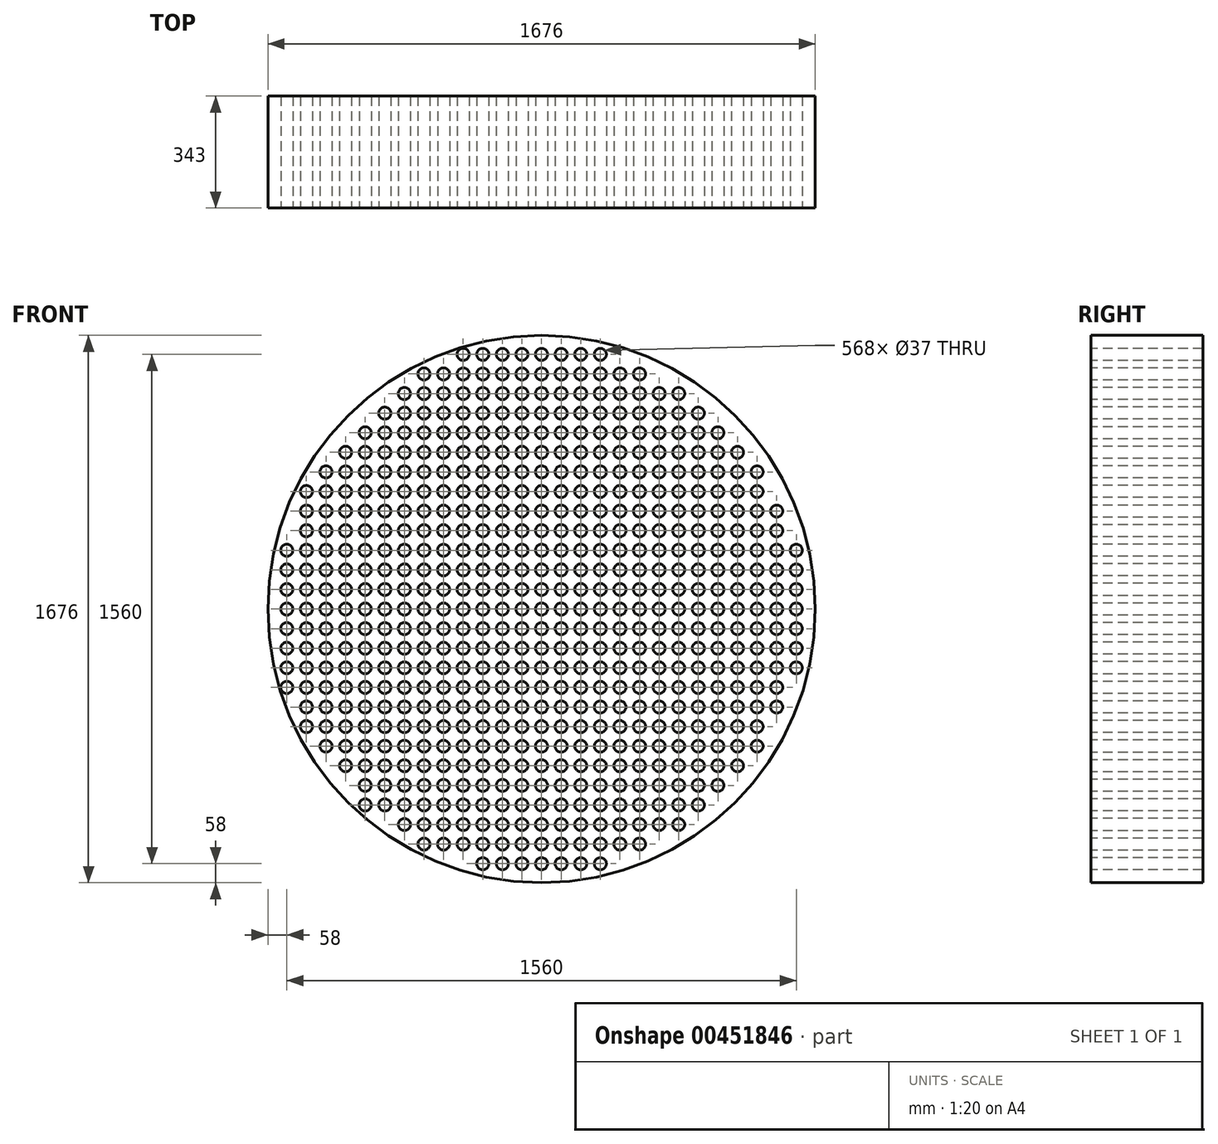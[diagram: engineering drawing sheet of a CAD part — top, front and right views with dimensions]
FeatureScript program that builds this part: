
annotation { "Feature Type Name" : "Feature", "Feature Type Description" : "" }
export const myFeature = defineFeature(function(context is Context, id is Id, definition is map)
    precondition{}
    {
        {
            var Q0;
            Q0=qCreatedBy(makeId("Front.planeOp"),FACE);
            var sketch = newSketch(context, id + "F0", { "sketchPlane" : qUnion([Q0])});
            skCircle(sketch, "E0", {"center": v(0, 0) * mm, "radius": 838 * mm});
            skSolve(sketch);
        }
        {
            var Q0;
            Q0 = qSketchRegion(id + "F0", true);
            extrude(context, id + "F1", {"entities" : qUnion([Q0]), "oppositeDirection" : true, "depth" : 343 * mm});
        }
        {
            var Q0;
            Q0=makeQuery(id+"F1.opExtrude","CAP_FACE",FACE,{"disambiguationData":[OSD([sQuery(id+"F0.wireOp",EDGE,"E0")])],"isStart":true});
            var sketch = newSketch(context, id + "F2", { "sketchPlane" : qUnion([Q0])});
            skCircle(sketch, "E1", {"center": v(0, 0) * mm, "radius": 18.5 * mm});
            skCircle(sketch, "E2.0.1.0", {"center": v(0, 60) * mm, "radius": 18.5 * mm});
            skCircle(sketch, "E2.0.2.0", {"center": v(0, 120) * mm, "radius": 18.5 * mm});
            skCircle(sketch, "E2.0.3.0", {"center": v(0, 180) * mm, "radius": 18.5 * mm});
            skCircle(sketch, "E2.0.4.0", {"center": v(0, 240) * mm, "radius": 18.5 * mm});
            skCircle(sketch, "E2.0.5.0", {"center": v(0, 300) * mm, "radius": 18.5 * mm});
            skCircle(sketch, "E2.0.6.0", {"center": v(0, 360) * mm, "radius": 18.5 * mm});
            skCircle(sketch, "E2.0.7.0", {"center": v(0, 420) * mm, "radius": 18.5 * mm});
            skCircle(sketch, "E2.0.8.0", {"center": v(0, 480) * mm, "radius": 18.5 * mm});
            skCircle(sketch, "E2.0.9.0", {"center": v(0, 540) * mm, "radius": 18.5 * mm});
            skCircle(sketch, "E2.0.10.0", {"center": v(0, 600) * mm, "radius": 18.5 * mm});
            skCircle(sketch, "E2.0.11.0", {"center": v(0, 660) * mm, "radius": 18.5 * mm});
            skCircle(sketch, "E2.0.12.0", {"center": v(0, 720) * mm, "radius": 18.5 * mm});
            skCircle(sketch, "E2.0.13.0", {"center": v(0, 780) * mm, "radius": 18.5 * mm});
            skCircle(sketch, "E2.1.0.0", {"center": v(60, 0) * mm, "radius": 18.5 * mm});
            skCircle(sketch, "E2.1.1.0", {"center": v(60, 60) * mm, "radius": 18.5 * mm});
            skCircle(sketch, "E2.1.2.0", {"center": v(60, 120) * mm, "radius": 18.5 * mm});
            skCircle(sketch, "E2.1.3.0", {"center": v(60, 180) * mm, "radius": 18.5 * mm});
            skCircle(sketch, "E2.1.4.0", {"center": v(60, 240) * mm, "radius": 18.5 * mm});
            skCircle(sketch, "E2.1.5.0", {"center": v(60, 300) * mm, "radius": 18.5 * mm});
            skCircle(sketch, "E2.1.6.0", {"center": v(60, 360) * mm, "radius": 18.5 * mm});
            skCircle(sketch, "E2.1.7.0", {"center": v(60, 420) * mm, "radius": 18.5 * mm});
            skCircle(sketch, "E2.1.8.0", {"center": v(60, 480) * mm, "radius": 18.5 * mm});
            skCircle(sketch, "E2.1.9.0", {"center": v(60, 540) * mm, "radius": 18.5 * mm});
            skCircle(sketch, "E2.1.10.0", {"center": v(60, 600) * mm, "radius": 18.5 * mm});
            skCircle(sketch, "E2.1.11.0", {"center": v(60, 660) * mm, "radius": 18.5 * mm});
            skCircle(sketch, "E2.1.12.0", {"center": v(60, 720) * mm, "radius": 18.5 * mm});
            skCircle(sketch, "E2.1.13.0", {"center": v(60, 780) * mm, "radius": 18.5 * mm});
            skCircle(sketch, "E2.2.0.0", {"center": v(120, 0) * mm, "radius": 18.5 * mm});
            skCircle(sketch, "E2.2.1.0", {"center": v(120, 60) * mm, "radius": 18.5 * mm});
            skCircle(sketch, "E2.2.2.0", {"center": v(120, 120) * mm, "radius": 18.5 * mm});
            skCircle(sketch, "E2.2.3.0", {"center": v(120, 180) * mm, "radius": 18.5 * mm});
            skCircle(sketch, "E2.2.4.0", {"center": v(120, 240) * mm, "radius": 18.5 * mm});
            skCircle(sketch, "E2.2.5.0", {"center": v(120, 300) * mm, "radius": 18.5 * mm});
            skCircle(sketch, "E2.2.6.0", {"center": v(120, 360) * mm, "radius": 18.5 * mm});
            skCircle(sketch, "E2.2.7.0", {"center": v(120, 420) * mm, "radius": 18.5 * mm});
            skCircle(sketch, "E2.2.8.0", {"center": v(120, 480) * mm, "radius": 18.5 * mm});
            skCircle(sketch, "E2.2.9.0", {"center": v(120, 540) * mm, "radius": 18.5 * mm});
            skCircle(sketch, "E2.2.10.0", {"center": v(120, 600) * mm, "radius": 18.5 * mm});
            skCircle(sketch, "E2.2.11.0", {"center": v(120, 660) * mm, "radius": 18.5 * mm});
            skCircle(sketch, "E2.2.12.0", {"center": v(120, 720) * mm, "radius": 18.5 * mm});
            skCircle(sketch, "E2.2.13.0", {"center": v(120, 780) * mm, "radius": 18.5 * mm});
            skCircle(sketch, "E2.3.0.0", {"center": v(180, 0) * mm, "radius": 18.5 * mm});
            skCircle(sketch, "E2.3.1.0", {"center": v(180, 60) * mm, "radius": 18.5 * mm});
            skCircle(sketch, "E2.3.2.0", {"center": v(180, 120) * mm, "radius": 18.5 * mm});
            skCircle(sketch, "E2.3.3.0", {"center": v(180, 180) * mm, "radius": 18.5 * mm});
            skCircle(sketch, "E2.3.4.0", {"center": v(180, 240) * mm, "radius": 18.5 * mm});
            skCircle(sketch, "E2.3.5.0", {"center": v(180, 300) * mm, "radius": 18.5 * mm});
            skCircle(sketch, "E2.3.6.0", {"center": v(180, 360) * mm, "radius": 18.5 * mm});
            skCircle(sketch, "E2.3.7.0", {"center": v(180, 420) * mm, "radius": 18.5 * mm});
            skCircle(sketch, "E2.3.8.0", {"center": v(180, 480) * mm, "radius": 18.5 * mm});
            skCircle(sketch, "E2.3.9.0", {"center": v(180, 540) * mm, "radius": 18.5 * mm});
            skCircle(sketch, "E2.3.10.0", {"center": v(180, 600) * mm, "radius": 18.5 * mm});
            skCircle(sketch, "E2.3.11.0", {"center": v(180, 660) * mm, "radius": 18.5 * mm});
            skCircle(sketch, "E2.3.12.0", {"center": v(180, 720) * mm, "radius": 18.5 * mm});
            skCircle(sketch, "E2.3.13.0", {"center": v(180, 780) * mm, "radius": 18.5 * mm});
            skCircle(sketch, "E2.4.0.0", {"center": v(240, 0) * mm, "radius": 18.5 * mm});
            skCircle(sketch, "E2.4.1.0", {"center": v(240, 60) * mm, "radius": 18.5 * mm});
            skCircle(sketch, "E2.4.2.0", {"center": v(240, 120) * mm, "radius": 18.5 * mm});
            skCircle(sketch, "E2.4.3.0", {"center": v(240, 180) * mm, "radius": 18.5 * mm});
            skCircle(sketch, "E2.4.4.0", {"center": v(240, 240) * mm, "radius": 18.5 * mm});
            skCircle(sketch, "E2.4.5.0", {"center": v(240, 300) * mm, "radius": 18.5 * mm});
            skCircle(sketch, "E2.4.6.0", {"center": v(240, 360) * mm, "radius": 18.5 * mm});
            skCircle(sketch, "E2.4.7.0", {"center": v(240, 420) * mm, "radius": 18.5 * mm});
            skCircle(sketch, "E2.4.8.0", {"center": v(240, 480) * mm, "radius": 18.5 * mm});
            skCircle(sketch, "E2.4.9.0", {"center": v(240, 540) * mm, "radius": 18.5 * mm});
            skCircle(sketch, "E2.4.10.0", {"center": v(240, 600) * mm, "radius": 18.5 * mm});
            skCircle(sketch, "E2.4.11.0", {"center": v(240, 660) * mm, "radius": 18.5 * mm});
            skCircle(sketch, "E2.4.12.0", {"center": v(240, 720) * mm, "radius": 18.5 * mm});
            skCircle(sketch, "E2.5.0.0", {"center": v(300, 0) * mm, "radius": 18.5 * mm});
            skCircle(sketch, "E2.5.1.0", {"center": v(300, 60) * mm, "radius": 18.5 * mm});
            skCircle(sketch, "E2.5.2.0", {"center": v(300, 120) * mm, "radius": 18.5 * mm});
            skCircle(sketch, "E2.5.3.0", {"center": v(300, 180) * mm, "radius": 18.5 * mm});
            skCircle(sketch, "E2.5.4.0", {"center": v(300, 240) * mm, "radius": 18.5 * mm});
            skCircle(sketch, "E2.5.5.0", {"center": v(300, 300) * mm, "radius": 18.5 * mm});
            skCircle(sketch, "E2.5.6.0", {"center": v(300, 360) * mm, "radius": 18.5 * mm});
            skCircle(sketch, "E2.5.7.0", {"center": v(300, 420) * mm, "radius": 18.5 * mm});
            skCircle(sketch, "E2.5.8.0", {"center": v(300, 480) * mm, "radius": 18.5 * mm});
            skCircle(sketch, "E2.5.9.0", {"center": v(300, 540) * mm, "radius": 18.5 * mm});
            skCircle(sketch, "E2.5.10.0", {"center": v(300, 600) * mm, "radius": 18.5 * mm});
            skCircle(sketch, "E2.5.11.0", {"center": v(300, 660) * mm, "radius": 18.5 * mm});
            skCircle(sketch, "E2.5.12.0", {"center": v(300, 720) * mm, "radius": 18.5 * mm});
            skCircle(sketch, "E2.6.0.0", {"center": v(360, 0) * mm, "radius": 18.5 * mm});
            skCircle(sketch, "E2.6.1.0", {"center": v(360, 60) * mm, "radius": 18.5 * mm});
            skCircle(sketch, "E2.6.2.0", {"center": v(360, 120) * mm, "radius": 18.5 * mm});
            skCircle(sketch, "E2.6.3.0", {"center": v(360, 180) * mm, "radius": 18.5 * mm});
            skCircle(sketch, "E2.6.4.0", {"center": v(360, 240) * mm, "radius": 18.5 * mm});
            skCircle(sketch, "E2.6.5.0", {"center": v(360, 300) * mm, "radius": 18.5 * mm});
            skCircle(sketch, "E2.6.6.0", {"center": v(360, 360) * mm, "radius": 18.5 * mm});
            skCircle(sketch, "E2.6.7.0", {"center": v(360, 420) * mm, "radius": 18.5 * mm});
            skCircle(sketch, "E2.6.8.0", {"center": v(360, 480) * mm, "radius": 18.5 * mm});
            skCircle(sketch, "E2.6.9.0", {"center": v(360, 540) * mm, "radius": 18.5 * mm});
            skCircle(sketch, "E2.6.10.0", {"center": v(360, 600) * mm, "radius": 18.5 * mm});
            skCircle(sketch, "E2.6.11.0", {"center": v(360, 660) * mm, "radius": 18.5 * mm});
            skCircle(sketch, "E2.7.0.0", {"center": v(420, 0) * mm, "radius": 18.5 * mm});
            skCircle(sketch, "E2.7.1.0", {"center": v(420, 60) * mm, "radius": 18.5 * mm});
            skCircle(sketch, "E2.7.2.0", {"center": v(420, 120) * mm, "radius": 18.5 * mm});
            skCircle(sketch, "E2.7.3.0", {"center": v(420, 180) * mm, "radius": 18.5 * mm});
            skCircle(sketch, "E2.7.4.0", {"center": v(420, 240) * mm, "radius": 18.5 * mm});
            skCircle(sketch, "E2.7.5.0", {"center": v(420, 300) * mm, "radius": 18.5 * mm});
            skCircle(sketch, "E2.7.6.0", {"center": v(420, 360) * mm, "radius": 18.5 * mm});
            skCircle(sketch, "E2.7.7.0", {"center": v(420, 420) * mm, "radius": 18.5 * mm});
            skCircle(sketch, "E2.7.8.0", {"center": v(420, 480) * mm, "radius": 18.5 * mm});
            skCircle(sketch, "E2.7.9.0", {"center": v(420, 540) * mm, "radius": 18.5 * mm});
            skCircle(sketch, "E2.7.10.0", {"center": v(420, 600) * mm, "radius": 18.5 * mm});
            skCircle(sketch, "E2.7.11.0", {"center": v(420, 660) * mm, "radius": 18.5 * mm});
            skCircle(sketch, "E2.8.0.0", {"center": v(480, 0) * mm, "radius": 18.5 * mm});
            skCircle(sketch, "E2.8.1.0", {"center": v(480, 60) * mm, "radius": 18.5 * mm});
            skCircle(sketch, "E2.8.2.0", {"center": v(480, 120) * mm, "radius": 18.5 * mm});
            skCircle(sketch, "E2.8.3.0", {"center": v(480, 180) * mm, "radius": 18.5 * mm});
            skCircle(sketch, "E2.8.4.0", {"center": v(480, 240) * mm, "radius": 18.5 * mm});
            skCircle(sketch, "E2.8.5.0", {"center": v(480, 300) * mm, "radius": 18.5 * mm});
            skCircle(sketch, "E2.8.6.0", {"center": v(480, 360) * mm, "radius": 18.5 * mm});
            skCircle(sketch, "E2.8.7.0", {"center": v(480, 420) * mm, "radius": 18.5 * mm});
            skCircle(sketch, "E2.8.8.0", {"center": v(480, 480) * mm, "radius": 18.5 * mm});
            skCircle(sketch, "E2.8.9.0", {"center": v(480, 540) * mm, "radius": 18.5 * mm});
            skCircle(sketch, "E2.8.10.0", {"center": v(480, 600) * mm, "radius": 18.5 * mm});
            skCircle(sketch, "E2.9.0.0", {"center": v(540, 0) * mm, "radius": 18.5 * mm});
            skCircle(sketch, "E2.9.1.0", {"center": v(540, 60) * mm, "radius": 18.5 * mm});
            skCircle(sketch, "E2.9.2.0", {"center": v(540, 120) * mm, "radius": 18.5 * mm});
            skCircle(sketch, "E2.9.3.0", {"center": v(540, 180) * mm, "radius": 18.5 * mm});
            skCircle(sketch, "E2.9.4.0", {"center": v(540, 240) * mm, "radius": 18.5 * mm});
            skCircle(sketch, "E2.9.5.0", {"center": v(540, 300) * mm, "radius": 18.5 * mm});
            skCircle(sketch, "E2.9.6.0", {"center": v(540, 360) * mm, "radius": 18.5 * mm});
            skCircle(sketch, "E2.9.7.0", {"center": v(540, 420) * mm, "radius": 18.5 * mm});
            skCircle(sketch, "E2.9.8.0", {"center": v(540, 480) * mm, "radius": 18.5 * mm});
            skCircle(sketch, "E2.9.9.0", {"center": v(540, 540) * mm, "radius": 18.5 * mm});
            skCircle(sketch, "E2.10.0.0", {"center": v(600, 0) * mm, "radius": 18.5 * mm});
            skCircle(sketch, "E2.10.1.0", {"center": v(600, 60) * mm, "radius": 18.5 * mm});
            skCircle(sketch, "E2.10.2.0", {"center": v(600, 120) * mm, "radius": 18.5 * mm});
            skCircle(sketch, "E2.10.3.0", {"center": v(600, 180) * mm, "radius": 18.5 * mm});
            skCircle(sketch, "E2.10.4.0", {"center": v(600, 240) * mm, "radius": 18.5 * mm});
            skCircle(sketch, "E2.10.5.0", {"center": v(600, 300) * mm, "radius": 18.5 * mm});
            skCircle(sketch, "E2.10.6.0", {"center": v(600, 360) * mm, "radius": 18.5 * mm});
            skCircle(sketch, "E2.10.7.0", {"center": v(600, 420) * mm, "radius": 18.5 * mm});
            skCircle(sketch, "E2.10.8.0", {"center": v(600, 480) * mm, "radius": 18.5 * mm});
            skCircle(sketch, "E2.11.0.0", {"center": v(660, 0) * mm, "radius": 18.5 * mm});
            skCircle(sketch, "E2.11.1.0", {"center": v(660, 60) * mm, "radius": 18.5 * mm});
            skCircle(sketch, "E2.11.2.0", {"center": v(660, 120) * mm, "radius": 18.5 * mm});
            skCircle(sketch, "E2.11.3.0", {"center": v(660, 180) * mm, "radius": 18.5 * mm});
            skCircle(sketch, "E2.11.4.0", {"center": v(660, 240) * mm, "radius": 18.5 * mm});
            skCircle(sketch, "E2.11.5.0", {"center": v(660, 300) * mm, "radius": 18.5 * mm});
            skCircle(sketch, "E2.11.6.0", {"center": v(660, 360) * mm, "radius": 18.5 * mm});
            skCircle(sketch, "E2.11.7.0", {"center": v(660, 420) * mm, "radius": 18.5 * mm});
            skCircle(sketch, "E2.12.0.0", {"center": v(720, 0) * mm, "radius": 18.5 * mm});
            skCircle(sketch, "E2.12.1.0", {"center": v(720, 60) * mm, "radius": 18.5 * mm});
            skCircle(sketch, "E2.12.2.0", {"center": v(720, 120) * mm, "radius": 18.5 * mm});
            skCircle(sketch, "E2.12.3.0", {"center": v(720, 180) * mm, "radius": 18.5 * mm});
            skCircle(sketch, "E2.12.4.0", {"center": v(720, 240) * mm, "radius": 18.5 * mm});
            skCircle(sketch, "E2.12.5.0", {"center": v(720, 300) * mm, "radius": 18.5 * mm});
            skCircle(sketch, "E2.13.0.0", {"center": v(780, 0) * mm, "radius": 18.5 * mm});
            skCircle(sketch, "E2.13.1.0", {"center": v(780, 60) * mm, "radius": 18.5 * mm});
            skCircle(sketch, "E2.13.2.0", {"center": v(780, 120) * mm, "radius": 18.5 * mm});
            skCircle(sketch, "E2.13.3.0", {"center": v(780, 180) * mm, "radius": 18.5 * mm});
            skLineSegment(sketch, "E2.direction1", {"start": v(0, 0) * mm, "end": v(60, 0) * mm, "construction": true});
            skLineSegment(sketch, "E2.direction2", {"start": v(0, 0) * mm, "end": v(0, 60) * mm, "construction": true});
            skCircle(sketch, "E3.0.1.0", {"center": v(0, -60) * mm, "radius": 18.5 * mm});
            skCircle(sketch, "E3.0.2.0", {"center": v(0, -120) * mm, "radius": 18.5 * mm});
            skCircle(sketch, "E3.0.3.0", {"center": v(0, -180) * mm, "radius": 18.5 * mm});
            skCircle(sketch, "E3.0.4.0", {"center": v(0, -240) * mm, "radius": 18.5 * mm});
            skCircle(sketch, "E3.0.5.0", {"center": v(0, -300) * mm, "radius": 18.5 * mm});
            skCircle(sketch, "E3.0.6.0", {"center": v(0, -360) * mm, "radius": 18.5 * mm});
            skCircle(sketch, "E3.0.7.0", {"center": v(0, -420) * mm, "radius": 18.5 * mm});
            skCircle(sketch, "E3.0.8.0", {"center": v(0, -480) * mm, "radius": 18.5 * mm});
            skCircle(sketch, "E3.0.9.0", {"center": v(0, -540) * mm, "radius": 18.5 * mm});
            skCircle(sketch, "E3.0.10.0", {"center": v(0, -600) * mm, "radius": 18.5 * mm});
            skCircle(sketch, "E3.0.11.0", {"center": v(0, -660) * mm, "radius": 18.5 * mm});
            skCircle(sketch, "E3.0.12.0", {"center": v(0, -720) * mm, "radius": 18.5 * mm});
            skCircle(sketch, "E3.0.13.0", {"center": v(0, -780) * mm, "radius": 18.5 * mm});
            skCircle(sketch, "E3.1.0.0", {"center": v(-60, 0) * mm, "radius": 18.5 * mm});
            skCircle(sketch, "E3.1.1.0", {"center": v(-60, -60) * mm, "radius": 18.5 * mm});
            skCircle(sketch, "E3.1.2.0", {"center": v(-60, -120) * mm, "radius": 18.5 * mm});
            skCircle(sketch, "E3.1.3.0", {"center": v(-60, -180) * mm, "radius": 18.5 * mm});
            skCircle(sketch, "E3.1.4.0", {"center": v(-60, -240) * mm, "radius": 18.5 * mm});
            skCircle(sketch, "E3.1.5.0", {"center": v(-60, -300) * mm, "radius": 18.5 * mm});
            skCircle(sketch, "E3.1.6.0", {"center": v(-60, -360) * mm, "radius": 18.5 * mm});
            skCircle(sketch, "E3.1.7.0", {"center": v(-60, -420) * mm, "radius": 18.5 * mm});
            skCircle(sketch, "E3.1.8.0", {"center": v(-60, -480) * mm, "radius": 18.5 * mm});
            skCircle(sketch, "E3.1.9.0", {"center": v(-60, -540) * mm, "radius": 18.5 * mm});
            skCircle(sketch, "E3.1.10.0", {"center": v(-60, -600) * mm, "radius": 18.5 * mm});
            skCircle(sketch, "E3.1.11.0", {"center": v(-60, -660) * mm, "radius": 18.5 * mm});
            skCircle(sketch, "E3.1.12.0", {"center": v(-60, -720) * mm, "radius": 18.5 * mm});
            skCircle(sketch, "E3.1.13.0", {"center": v(-60, -780) * mm, "radius": 18.5 * mm});
            skCircle(sketch, "E3.2.0.0", {"center": v(-120, 0) * mm, "radius": 18.5 * mm});
            skCircle(sketch, "E3.2.1.0", {"center": v(-120, -60) * mm, "radius": 18.5 * mm});
            skCircle(sketch, "E3.2.2.0", {"center": v(-120, -120) * mm, "radius": 18.5 * mm});
            skCircle(sketch, "E3.2.3.0", {"center": v(-120, -180) * mm, "radius": 18.5 * mm});
            skCircle(sketch, "E3.2.4.0", {"center": v(-120, -240) * mm, "radius": 18.5 * mm});
            skCircle(sketch, "E3.2.5.0", {"center": v(-120, -300) * mm, "radius": 18.5 * mm});
            skCircle(sketch, "E3.2.6.0", {"center": v(-120, -360) * mm, "radius": 18.5 * mm});
            skCircle(sketch, "E3.2.7.0", {"center": v(-120, -420) * mm, "radius": 18.5 * mm});
            skCircle(sketch, "E3.2.8.0", {"center": v(-120, -480) * mm, "radius": 18.5 * mm});
            skCircle(sketch, "E3.2.9.0", {"center": v(-120, -540) * mm, "radius": 18.5 * mm});
            skCircle(sketch, "E3.2.10.0", {"center": v(-120, -600) * mm, "radius": 18.5 * mm});
            skCircle(sketch, "E3.2.11.0", {"center": v(-120, -660) * mm, "radius": 18.5 * mm});
            skCircle(sketch, "E3.2.12.0", {"center": v(-120, -720) * mm, "radius": 18.5 * mm});
            skCircle(sketch, "E3.2.13.0", {"center": v(-120, -780) * mm, "radius": 18.5 * mm});
            skCircle(sketch, "E3.3.0.0", {"center": v(-180, 0) * mm, "radius": 18.5 * mm});
            skCircle(sketch, "E3.3.1.0", {"center": v(-180, -60) * mm, "radius": 18.5 * mm});
            skCircle(sketch, "E3.3.2.0", {"center": v(-180, -120) * mm, "radius": 18.5 * mm});
            skCircle(sketch, "E3.3.3.0", {"center": v(-180, -180) * mm, "radius": 18.5 * mm});
            skCircle(sketch, "E3.3.4.0", {"center": v(-180, -240) * mm, "radius": 18.5 * mm});
            skCircle(sketch, "E3.3.5.0", {"center": v(-180, -300) * mm, "radius": 18.5 * mm});
            skCircle(sketch, "E3.3.6.0", {"center": v(-180, -360) * mm, "radius": 18.5 * mm});
            skCircle(sketch, "E3.3.7.0", {"center": v(-180, -420) * mm, "radius": 18.5 * mm});
            skCircle(sketch, "E3.3.8.0", {"center": v(-180, -480) * mm, "radius": 18.5 * mm});
            skCircle(sketch, "E3.3.9.0", {"center": v(-180, -540) * mm, "radius": 18.5 * mm});
            skCircle(sketch, "E3.3.10.0", {"center": v(-180, -600) * mm, "radius": 18.5 * mm});
            skCircle(sketch, "E3.3.11.0", {"center": v(-180, -660) * mm, "radius": 18.5 * mm});
            skCircle(sketch, "E3.3.12.0", {"center": v(-180, -720) * mm, "radius": 18.5 * mm});
            skCircle(sketch, "E3.3.13.0", {"center": v(-180, -780) * mm, "radius": 18.5 * mm});
            skCircle(sketch, "E3.4.0.0", {"center": v(-240, 0) * mm, "radius": 18.5 * mm});
            skCircle(sketch, "E3.4.1.0", {"center": v(-240, -60) * mm, "radius": 18.5 * mm});
            skCircle(sketch, "E3.4.2.0", {"center": v(-240, -120) * mm, "radius": 18.5 * mm});
            skCircle(sketch, "E3.4.3.0", {"center": v(-240, -180) * mm, "radius": 18.5 * mm});
            skCircle(sketch, "E3.4.4.0", {"center": v(-240, -240) * mm, "radius": 18.5 * mm});
            skCircle(sketch, "E3.4.5.0", {"center": v(-240, -300) * mm, "radius": 18.5 * mm});
            skCircle(sketch, "E3.4.6.0", {"center": v(-240, -360) * mm, "radius": 18.5 * mm});
            skCircle(sketch, "E3.4.7.0", {"center": v(-240, -420) * mm, "radius": 18.5 * mm});
            skCircle(sketch, "E3.4.8.0", {"center": v(-240, -480) * mm, "radius": 18.5 * mm});
            skCircle(sketch, "E3.4.9.0", {"center": v(-240, -540) * mm, "radius": 18.5 * mm});
            skCircle(sketch, "E3.4.10.0", {"center": v(-240, -600) * mm, "radius": 18.5 * mm});
            skCircle(sketch, "E3.4.11.0", {"center": v(-240, -660) * mm, "radius": 18.5 * mm});
            skCircle(sketch, "E3.4.12.0", {"center": v(-240, -720) * mm, "radius": 18.5 * mm});
            skCircle(sketch, "E3.5.0.0", {"center": v(-300, 0) * mm, "radius": 18.5 * mm});
            skCircle(sketch, "E3.5.1.0", {"center": v(-300, -60) * mm, "radius": 18.5 * mm});
            skCircle(sketch, "E3.5.2.0", {"center": v(-300, -120) * mm, "radius": 18.5 * mm});
            skCircle(sketch, "E3.5.3.0", {"center": v(-300, -180) * mm, "radius": 18.5 * mm});
            skCircle(sketch, "E3.5.4.0", {"center": v(-300, -240) * mm, "radius": 18.5 * mm});
            skCircle(sketch, "E3.5.5.0", {"center": v(-300, -300) * mm, "radius": 18.5 * mm});
            skCircle(sketch, "E3.5.6.0", {"center": v(-300, -360) * mm, "radius": 18.5 * mm});
            skCircle(sketch, "E3.5.7.0", {"center": v(-300, -420) * mm, "radius": 18.5 * mm});
            skCircle(sketch, "E3.5.8.0", {"center": v(-300, -480) * mm, "radius": 18.5 * mm});
            skCircle(sketch, "E3.5.9.0", {"center": v(-300, -540) * mm, "radius": 18.5 * mm});
            skCircle(sketch, "E3.5.10.0", {"center": v(-300, -600) * mm, "radius": 18.5 * mm});
            skCircle(sketch, "E3.5.11.0", {"center": v(-300, -660) * mm, "radius": 18.5 * mm});
            skCircle(sketch, "E3.5.12.0", {"center": v(-300, -720) * mm, "radius": 18.5 * mm});
            skCircle(sketch, "E3.6.0.0", {"center": v(-360, 0) * mm, "radius": 18.5 * mm});
            skCircle(sketch, "E3.6.1.0", {"center": v(-360, -60) * mm, "radius": 18.5 * mm});
            skCircle(sketch, "E3.6.2.0", {"center": v(-360, -120) * mm, "radius": 18.5 * mm});
            skCircle(sketch, "E3.6.3.0", {"center": v(-360, -180) * mm, "radius": 18.5 * mm});
            skCircle(sketch, "E3.6.4.0", {"center": v(-360, -240) * mm, "radius": 18.5 * mm});
            skCircle(sketch, "E3.6.5.0", {"center": v(-360, -300) * mm, "radius": 18.5 * mm});
            skCircle(sketch, "E3.6.6.0", {"center": v(-360, -360) * mm, "radius": 18.5 * mm});
            skCircle(sketch, "E3.6.7.0", {"center": v(-360, -420) * mm, "radius": 18.5 * mm});
            skCircle(sketch, "E3.6.8.0", {"center": v(-360, -480) * mm, "radius": 18.5 * mm});
            skCircle(sketch, "E3.6.9.0", {"center": v(-360, -540) * mm, "radius": 18.5 * mm});
            skCircle(sketch, "E3.6.10.0", {"center": v(-360, -600) * mm, "radius": 18.5 * mm});
            skCircle(sketch, "E3.6.11.0", {"center": v(-360, -660) * mm, "radius": 18.5 * mm});
            skCircle(sketch, "E3.6.12.0", {"center": v(-360, -720) * mm, "radius": 18.5 * mm});
            skCircle(sketch, "E3.7.0.0", {"center": v(-420, 0) * mm, "radius": 18.5 * mm});
            skCircle(sketch, "E3.7.1.0", {"center": v(-420, -60) * mm, "radius": 18.5 * mm});
            skCircle(sketch, "E3.7.2.0", {"center": v(-420, -120) * mm, "radius": 18.5 * mm});
            skCircle(sketch, "E3.7.3.0", {"center": v(-420, -180) * mm, "radius": 18.5 * mm});
            skCircle(sketch, "E3.7.4.0", {"center": v(-420, -240) * mm, "radius": 18.5 * mm});
            skCircle(sketch, "E3.7.5.0", {"center": v(-420, -300) * mm, "radius": 18.5 * mm});
            skCircle(sketch, "E3.7.6.0", {"center": v(-420, -360) * mm, "radius": 18.5 * mm});
            skCircle(sketch, "E3.7.7.0", {"center": v(-420, -420) * mm, "radius": 18.5 * mm});
            skCircle(sketch, "E3.7.8.0", {"center": v(-420, -480) * mm, "radius": 18.5 * mm});
            skCircle(sketch, "E3.7.9.0", {"center": v(-420, -540) * mm, "radius": 18.5 * mm});
            skCircle(sketch, "E3.7.10.0", {"center": v(-420, -600) * mm, "radius": 18.5 * mm});
            skCircle(sketch, "E3.7.11.0", {"center": v(-420, -660) * mm, "radius": 18.5 * mm});
            skCircle(sketch, "E3.8.0.0", {"center": v(-480, 0) * mm, "radius": 18.5 * mm});
            skCircle(sketch, "E3.8.1.0", {"center": v(-480, -60) * mm, "radius": 18.5 * mm});
            skCircle(sketch, "E3.8.2.0", {"center": v(-480, -120) * mm, "radius": 18.5 * mm});
            skCircle(sketch, "E3.8.3.0", {"center": v(-480, -180) * mm, "radius": 18.5 * mm});
            skCircle(sketch, "E3.8.4.0", {"center": v(-480, -240) * mm, "radius": 18.5 * mm});
            skCircle(sketch, "E3.8.5.0", {"center": v(-480, -300) * mm, "radius": 18.5 * mm});
            skCircle(sketch, "E3.8.6.0", {"center": v(-480, -360) * mm, "radius": 18.5 * mm});
            skCircle(sketch, "E3.8.7.0", {"center": v(-480, -420) * mm, "radius": 18.5 * mm});
            skCircle(sketch, "E3.8.8.0", {"center": v(-480, -480) * mm, "radius": 18.5 * mm});
            skCircle(sketch, "E3.8.9.0", {"center": v(-480, -540) * mm, "radius": 18.5 * mm});
            skCircle(sketch, "E3.8.10.0", {"center": v(-480, -600) * mm, "radius": 18.5 * mm});
            skCircle(sketch, "E3.9.0.0", {"center": v(-540, 0) * mm, "radius": 18.5 * mm});
            skCircle(sketch, "E3.9.1.0", {"center": v(-540, -60) * mm, "radius": 18.5 * mm});
            skCircle(sketch, "E3.9.2.0", {"center": v(-540, -120) * mm, "radius": 18.5 * mm});
            skCircle(sketch, "E3.9.3.0", {"center": v(-540, -180) * mm, "radius": 18.5 * mm});
            skCircle(sketch, "E3.9.4.0", {"center": v(-540, -240) * mm, "radius": 18.5 * mm});
            skCircle(sketch, "E3.9.5.0", {"center": v(-540, -300) * mm, "radius": 18.5 * mm});
            skCircle(sketch, "E3.9.6.0", {"center": v(-540, -360) * mm, "radius": 18.5 * mm});
            skCircle(sketch, "E3.9.7.0", {"center": v(-540, -420) * mm, "radius": 18.5 * mm});
            skCircle(sketch, "E3.9.8.0", {"center": v(-540, -480) * mm, "radius": 18.5 * mm});
            skCircle(sketch, "E3.9.9.0", {"center": v(-540, -540) * mm, "radius": 18.5 * mm});
            skCircle(sketch, "E3.9.10.0", {"center": v(-540, -600) * mm, "radius": 18.5 * mm});
            skCircle(sketch, "E3.10.0.0", {"center": v(-600, 0) * mm, "radius": 18.5 * mm});
            skCircle(sketch, "E3.10.1.0", {"center": v(-600, -60) * mm, "radius": 18.5 * mm});
            skCircle(sketch, "E3.10.2.0", {"center": v(-600, -120) * mm, "radius": 18.5 * mm});
            skCircle(sketch, "E3.10.3.0", {"center": v(-600, -180) * mm, "radius": 18.5 * mm});
            skCircle(sketch, "E3.10.4.0", {"center": v(-600, -240) * mm, "radius": 18.5 * mm});
            skCircle(sketch, "E3.10.5.0", {"center": v(-600, -300) * mm, "radius": 18.5 * mm});
            skCircle(sketch, "E3.10.6.0", {"center": v(-600, -360) * mm, "radius": 18.5 * mm});
            skCircle(sketch, "E3.10.7.0", {"center": v(-600, -420) * mm, "radius": 18.5 * mm});
            skCircle(sketch, "E3.10.8.0", {"center": v(-600, -480) * mm, "radius": 18.5 * mm});
            skCircle(sketch, "E3.11.0.0", {"center": v(-660, 0) * mm, "radius": 18.5 * mm});
            skCircle(sketch, "E3.11.1.0", {"center": v(-660, -60) * mm, "radius": 18.5 * mm});
            skCircle(sketch, "E3.11.2.0", {"center": v(-660, -120) * mm, "radius": 18.5 * mm});
            skCircle(sketch, "E3.11.3.0", {"center": v(-660, -180) * mm, "radius": 18.5 * mm});
            skCircle(sketch, "E3.11.4.0", {"center": v(-660, -240) * mm, "radius": 18.5 * mm});
            skCircle(sketch, "E3.11.5.0", {"center": v(-660, -300) * mm, "radius": 18.5 * mm});
            skCircle(sketch, "E3.11.6.0", {"center": v(-660, -360) * mm, "radius": 18.5 * mm});
            skCircle(sketch, "E3.11.7.0", {"center": v(-660, -420) * mm, "radius": 18.5 * mm});
            skCircle(sketch, "E3.12.0.0", {"center": v(-720, 0) * mm, "radius": 18.5 * mm});
            skCircle(sketch, "E3.12.1.0", {"center": v(-720, -60) * mm, "radius": 18.5 * mm});
            skCircle(sketch, "E3.12.2.0", {"center": v(-720, -120) * mm, "radius": 18.5 * mm});
            skCircle(sketch, "E3.12.3.0", {"center": v(-720, -180) * mm, "radius": 18.5 * mm});
            skCircle(sketch, "E3.12.4.0", {"center": v(-720, -240) * mm, "radius": 18.5 * mm});
            skCircle(sketch, "E3.12.5.0", {"center": v(-720, -300) * mm, "radius": 18.5 * mm});
            skCircle(sketch, "E3.12.6.0", {"center": v(-720, -360) * mm, "radius": 18.5 * mm});
            skCircle(sketch, "E3.13.0.0", {"center": v(-780, 0) * mm, "radius": 18.5 * mm});
            skCircle(sketch, "E3.13.1.0", {"center": v(-780, -60) * mm, "radius": 18.5 * mm});
            skCircle(sketch, "E3.13.2.0", {"center": v(-780, -120) * mm, "radius": 18.5 * mm});
            skCircle(sketch, "E3.13.3.0", {"center": v(-780, -180) * mm, "radius": 18.5 * mm});
            skCircle(sketch, "E3.13.4.0", {"center": v(-780, -240) * mm, "radius": 18.5 * mm});
            skLineSegment(sketch, "E3.direction1", {"start": v(-60, 0) * mm, "end": v(0, 0) * mm, "construction": true});
            skLineSegment(sketch, "E3.direction2", {"start": v(0, 0) * mm, "end": v(0, -60) * mm, "construction": true});
            skCircle(sketch, "E4.1.1.0", {"center": v(60, -60) * mm, "radius": 18.5 * mm});
            skCircle(sketch, "E4.1.2.0", {"center": v(60, -120) * mm, "radius": 18.5 * mm});
            skCircle(sketch, "E4.1.3.0", {"center": v(60, -180) * mm, "radius": 18.5 * mm});
            skCircle(sketch, "E4.1.4.0", {"center": v(60, -240) * mm, "radius": 18.5 * mm});
            skCircle(sketch, "E4.1.5.0", {"center": v(60, -300) * mm, "radius": 18.5 * mm});
            skCircle(sketch, "E4.1.6.0", {"center": v(60, -360) * mm, "radius": 18.5 * mm});
            skCircle(sketch, "E4.1.7.0", {"center": v(60, -420) * mm, "radius": 18.5 * mm});
            skCircle(sketch, "E4.1.8.0", {"center": v(60, -480) * mm, "radius": 18.5 * mm});
            skCircle(sketch, "E4.1.9.0", {"center": v(60, -540) * mm, "radius": 18.5 * mm});
            skCircle(sketch, "E4.1.10.0", {"center": v(60, -600) * mm, "radius": 18.5 * mm});
            skCircle(sketch, "E4.1.11.0", {"center": v(60, -660) * mm, "radius": 18.5 * mm});
            skCircle(sketch, "E4.1.12.0", {"center": v(60, -720) * mm, "radius": 18.5 * mm});
            skCircle(sketch, "E4.1.13.0", {"center": v(60, -780) * mm, "radius": 18.5 * mm});
            skCircle(sketch, "E4.2.1.0", {"center": v(120, -60) * mm, "radius": 18.5 * mm});
            skCircle(sketch, "E4.2.2.0", {"center": v(120, -120) * mm, "radius": 18.5 * mm});
            skCircle(sketch, "E4.2.3.0", {"center": v(120, -180) * mm, "radius": 18.5 * mm});
            skCircle(sketch, "E4.2.4.0", {"center": v(120, -240) * mm, "radius": 18.5 * mm});
            skCircle(sketch, "E4.2.5.0", {"center": v(120, -300) * mm, "radius": 18.5 * mm});
            skCircle(sketch, "E4.2.6.0", {"center": v(120, -360) * mm, "radius": 18.5 * mm});
            skCircle(sketch, "E4.2.7.0", {"center": v(120, -420) * mm, "radius": 18.5 * mm});
            skCircle(sketch, "E4.2.8.0", {"center": v(120, -480) * mm, "radius": 18.5 * mm});
            skCircle(sketch, "E4.2.9.0", {"center": v(120, -540) * mm, "radius": 18.5 * mm});
            skCircle(sketch, "E4.2.10.0", {"center": v(120, -600) * mm, "radius": 18.5 * mm});
            skCircle(sketch, "E4.2.11.0", {"center": v(120, -660) * mm, "radius": 18.5 * mm});
            skCircle(sketch, "E4.2.12.0", {"center": v(120, -720) * mm, "radius": 18.5 * mm});
            skCircle(sketch, "E4.2.13.0", {"center": v(120, -780) * mm, "radius": 18.5 * mm});
            skCircle(sketch, "E4.3.1.0", {"center": v(180, -60) * mm, "radius": 18.5 * mm});
            skCircle(sketch, "E4.3.2.0", {"center": v(180, -120) * mm, "radius": 18.5 * mm});
            skCircle(sketch, "E4.3.3.0", {"center": v(180, -180) * mm, "radius": 18.5 * mm});
            skCircle(sketch, "E4.3.4.0", {"center": v(180, -240) * mm, "radius": 18.5 * mm});
            skCircle(sketch, "E4.3.5.0", {"center": v(180, -300) * mm, "radius": 18.5 * mm});
            skCircle(sketch, "E4.3.6.0", {"center": v(180, -360) * mm, "radius": 18.5 * mm});
            skCircle(sketch, "E4.3.7.0", {"center": v(180, -420) * mm, "radius": 18.5 * mm});
            skCircle(sketch, "E4.3.8.0", {"center": v(180, -480) * mm, "radius": 18.5 * mm});
            skCircle(sketch, "E4.3.9.0", {"center": v(180, -540) * mm, "radius": 18.5 * mm});
            skCircle(sketch, "E4.3.10.0", {"center": v(180, -600) * mm, "radius": 18.5 * mm});
            skCircle(sketch, "E4.3.11.0", {"center": v(180, -660) * mm, "radius": 18.5 * mm});
            skCircle(sketch, "E4.3.12.0", {"center": v(180, -720) * mm, "radius": 18.5 * mm});
            skCircle(sketch, "E4.3.13.0", {"center": v(180, -780) * mm, "radius": 18.5 * mm});
            skCircle(sketch, "E4.4.1.0", {"center": v(240, -60) * mm, "radius": 18.5 * mm});
            skCircle(sketch, "E4.4.2.0", {"center": v(240, -120) * mm, "radius": 18.5 * mm});
            skCircle(sketch, "E4.4.3.0", {"center": v(240, -180) * mm, "radius": 18.5 * mm});
            skCircle(sketch, "E4.4.4.0", {"center": v(240, -240) * mm, "radius": 18.5 * mm});
            skCircle(sketch, "E4.4.5.0", {"center": v(240, -300) * mm, "radius": 18.5 * mm});
            skCircle(sketch, "E4.4.6.0", {"center": v(240, -360) * mm, "radius": 18.5 * mm});
            skCircle(sketch, "E4.4.7.0", {"center": v(240, -420) * mm, "radius": 18.5 * mm});
            skCircle(sketch, "E4.4.8.0", {"center": v(240, -480) * mm, "radius": 18.5 * mm});
            skCircle(sketch, "E4.4.9.0", {"center": v(240, -540) * mm, "radius": 18.5 * mm});
            skCircle(sketch, "E4.4.10.0", {"center": v(240, -600) * mm, "radius": 18.5 * mm});
            skCircle(sketch, "E4.4.11.0", {"center": v(240, -660) * mm, "radius": 18.5 * mm});
            skCircle(sketch, "E4.4.12.0", {"center": v(240, -720) * mm, "radius": 18.5 * mm});
            skCircle(sketch, "E4.5.1.0", {"center": v(300, -60) * mm, "radius": 18.5 * mm});
            skCircle(sketch, "E4.5.2.0", {"center": v(300, -120) * mm, "radius": 18.5 * mm});
            skCircle(sketch, "E4.5.3.0", {"center": v(300, -180) * mm, "radius": 18.5 * mm});
            skCircle(sketch, "E4.5.4.0", {"center": v(300, -240) * mm, "radius": 18.5 * mm});
            skCircle(sketch, "E4.5.5.0", {"center": v(300, -300) * mm, "radius": 18.5 * mm});
            skCircle(sketch, "E4.5.6.0", {"center": v(300, -360) * mm, "radius": 18.5 * mm});
            skCircle(sketch, "E4.5.7.0", {"center": v(300, -420) * mm, "radius": 18.5 * mm});
            skCircle(sketch, "E4.5.8.0", {"center": v(300, -480) * mm, "radius": 18.5 * mm});
            skCircle(sketch, "E4.5.9.0", {"center": v(300, -540) * mm, "radius": 18.5 * mm});
            skCircle(sketch, "E4.5.10.0", {"center": v(300, -600) * mm, "radius": 18.5 * mm});
            skCircle(sketch, "E4.5.11.0", {"center": v(300, -660) * mm, "radius": 18.5 * mm});
            skCircle(sketch, "E4.5.12.0", {"center": v(300, -720) * mm, "radius": 18.5 * mm});
            skCircle(sketch, "E4.6.1.0", {"center": v(360, -60) * mm, "radius": 18.5 * mm});
            skCircle(sketch, "E4.6.2.0", {"center": v(360, -120) * mm, "radius": 18.5 * mm});
            skCircle(sketch, "E4.6.3.0", {"center": v(360, -180) * mm, "radius": 18.5 * mm});
            skCircle(sketch, "E4.6.4.0", {"center": v(360, -240) * mm, "radius": 18.5 * mm});
            skCircle(sketch, "E4.6.5.0", {"center": v(360, -300) * mm, "radius": 18.5 * mm});
            skCircle(sketch, "E4.6.6.0", {"center": v(360, -360) * mm, "radius": 18.5 * mm});
            skCircle(sketch, "E4.6.7.0", {"center": v(360, -420) * mm, "radius": 18.5 * mm});
            skCircle(sketch, "E4.6.8.0", {"center": v(360, -480) * mm, "radius": 18.5 * mm});
            skCircle(sketch, "E4.6.9.0", {"center": v(360, -540) * mm, "radius": 18.5 * mm});
            skCircle(sketch, "E4.6.10.0", {"center": v(360, -600) * mm, "radius": 18.5 * mm});
            skCircle(sketch, "E4.6.11.0", {"center": v(360, -660) * mm, "radius": 18.5 * mm});
            skCircle(sketch, "E4.7.1.0", {"center": v(420, -60) * mm, "radius": 18.5 * mm});
            skCircle(sketch, "E4.7.2.0", {"center": v(420, -120) * mm, "radius": 18.5 * mm});
            skCircle(sketch, "E4.7.3.0", {"center": v(420, -180) * mm, "radius": 18.5 * mm});
            skCircle(sketch, "E4.7.4.0", {"center": v(420, -240) * mm, "radius": 18.5 * mm});
            skCircle(sketch, "E4.7.5.0", {"center": v(420, -300) * mm, "radius": 18.5 * mm});
            skCircle(sketch, "E4.7.6.0", {"center": v(420, -360) * mm, "radius": 18.5 * mm});
            skCircle(sketch, "E4.7.7.0", {"center": v(420, -420) * mm, "radius": 18.5 * mm});
            skCircle(sketch, "E4.7.8.0", {"center": v(420, -480) * mm, "radius": 18.5 * mm});
            skCircle(sketch, "E4.7.9.0", {"center": v(420, -540) * mm, "radius": 18.5 * mm});
            skCircle(sketch, "E4.7.10.0", {"center": v(420, -600) * mm, "radius": 18.5 * mm});
            skCircle(sketch, "E4.7.11.0", {"center": v(420, -660) * mm, "radius": 18.5 * mm});
            skCircle(sketch, "E4.8.1.0", {"center": v(480, -60) * mm, "radius": 18.5 * mm});
            skCircle(sketch, "E4.8.2.0", {"center": v(480, -120) * mm, "radius": 18.5 * mm});
            skCircle(sketch, "E4.8.3.0", {"center": v(480, -180) * mm, "radius": 18.5 * mm});
            skCircle(sketch, "E4.8.4.0", {"center": v(480, -240) * mm, "radius": 18.5 * mm});
            skCircle(sketch, "E4.8.5.0", {"center": v(480, -300) * mm, "radius": 18.5 * mm});
            skCircle(sketch, "E4.8.6.0", {"center": v(480, -360) * mm, "radius": 18.5 * mm});
            skCircle(sketch, "E4.8.7.0", {"center": v(480, -420) * mm, "radius": 18.5 * mm});
            skCircle(sketch, "E4.8.8.0", {"center": v(480, -480) * mm, "radius": 18.5 * mm});
            skCircle(sketch, "E4.8.9.0", {"center": v(480, -540) * mm, "radius": 18.5 * mm});
            skCircle(sketch, "E4.8.10.0", {"center": v(480, -600) * mm, "radius": 18.5 * mm});
            skCircle(sketch, "E4.9.1.0", {"center": v(540, -60) * mm, "radius": 18.5 * mm});
            skCircle(sketch, "E4.9.2.0", {"center": v(540, -120) * mm, "radius": 18.5 * mm});
            skCircle(sketch, "E4.9.3.0", {"center": v(540, -180) * mm, "radius": 18.5 * mm});
            skCircle(sketch, "E4.9.4.0", {"center": v(540, -240) * mm, "radius": 18.5 * mm});
            skCircle(sketch, "E4.9.5.0", {"center": v(540, -300) * mm, "radius": 18.5 * mm});
            skCircle(sketch, "E4.9.6.0", {"center": v(540, -360) * mm, "radius": 18.5 * mm});
            skCircle(sketch, "E4.9.7.0", {"center": v(540, -420) * mm, "radius": 18.5 * mm});
            skCircle(sketch, "E4.9.8.0", {"center": v(540, -480) * mm, "radius": 18.5 * mm});
            skCircle(sketch, "E4.9.9.0", {"center": v(540, -540) * mm, "radius": 18.5 * mm});
            skCircle(sketch, "E4.10.1.0", {"center": v(600, -60) * mm, "radius": 18.5 * mm});
            skCircle(sketch, "E4.10.2.0", {"center": v(600, -120) * mm, "radius": 18.5 * mm});
            skCircle(sketch, "E4.10.3.0", {"center": v(600, -180) * mm, "radius": 18.5 * mm});
            skCircle(sketch, "E4.10.4.0", {"center": v(600, -240) * mm, "radius": 18.5 * mm});
            skCircle(sketch, "E4.10.5.0", {"center": v(600, -300) * mm, "radius": 18.5 * mm});
            skCircle(sketch, "E4.10.6.0", {"center": v(600, -360) * mm, "radius": 18.5 * mm});
            skCircle(sketch, "E4.10.7.0", {"center": v(600, -420) * mm, "radius": 18.5 * mm});
            skCircle(sketch, "E4.10.8.0", {"center": v(600, -480) * mm, "radius": 18.5 * mm});
            skCircle(sketch, "E4.11.1.0", {"center": v(660, -60) * mm, "radius": 18.5 * mm});
            skCircle(sketch, "E4.11.2.0", {"center": v(660, -120) * mm, "radius": 18.5 * mm});
            skCircle(sketch, "E4.11.3.0", {"center": v(660, -180) * mm, "radius": 18.5 * mm});
            skCircle(sketch, "E4.11.4.0", {"center": v(660, -240) * mm, "radius": 18.5 * mm});
            skCircle(sketch, "E4.11.5.0", {"center": v(660, -300) * mm, "radius": 18.5 * mm});
            skCircle(sketch, "E4.11.6.0", {"center": v(660, -360) * mm, "radius": 18.5 * mm});
            skCircle(sketch, "E4.11.7.0", {"center": v(660, -420) * mm, "radius": 18.5 * mm});
            skCircle(sketch, "E4.12.1.0", {"center": v(720, -60) * mm, "radius": 18.5 * mm});
            skCircle(sketch, "E4.12.2.0", {"center": v(720, -120) * mm, "radius": 18.5 * mm});
            skCircle(sketch, "E4.12.3.0", {"center": v(720, -180) * mm, "radius": 18.5 * mm});
            skCircle(sketch, "E4.12.4.0", {"center": v(720, -240) * mm, "radius": 18.5 * mm});
            skCircle(sketch, "E4.12.5.0", {"center": v(720, -300) * mm, "radius": 18.5 * mm});
            skCircle(sketch, "E4.13.1.0", {"center": v(780, -60) * mm, "radius": 18.5 * mm});
            skCircle(sketch, "E4.13.2.0", {"center": v(780, -120) * mm, "radius": 18.5 * mm});
            skCircle(sketch, "E4.13.3.0", {"center": v(780, -180) * mm, "radius": 18.5 * mm});
            skLineSegment(sketch, "E4.direction1", {"start": v(60, 0) * mm, "end": v(0, 0) * mm, "construction": true});
            skLineSegment(sketch, "E4.direction2", {"start": v(0, -60) * mm, "end": v(0, 0) * mm, "construction": true});
            skCircle(sketch, "E5.1.1.0", {"center": v(-60, 60) * mm, "radius": 18.5 * mm});
            skCircle(sketch, "E5.1.2.0", {"center": v(-60, 120) * mm, "radius": 18.5 * mm});
            skCircle(sketch, "E5.1.3.0", {"center": v(-60, 180) * mm, "radius": 18.5 * mm});
            skCircle(sketch, "E5.1.4.0", {"center": v(-60, 240) * mm, "radius": 18.5 * mm});
            skCircle(sketch, "E5.1.5.0", {"center": v(-60, 300) * mm, "radius": 18.5 * mm});
            skCircle(sketch, "E5.1.6.0", {"center": v(-60, 360) * mm, "radius": 18.5 * mm});
            skCircle(sketch, "E5.1.7.0", {"center": v(-60, 420) * mm, "radius": 18.5 * mm});
            skCircle(sketch, "E5.1.8.0", {"center": v(-60, 480) * mm, "radius": 18.5 * mm});
            skCircle(sketch, "E5.1.9.0", {"center": v(-60, 540) * mm, "radius": 18.5 * mm});
            skCircle(sketch, "E5.1.10.0", {"center": v(-60, 600) * mm, "radius": 18.5 * mm});
            skCircle(sketch, "E5.1.11.0", {"center": v(-60, 660) * mm, "radius": 18.5 * mm});
            skCircle(sketch, "E5.1.12.0", {"center": v(-60, 720) * mm, "radius": 18.5 * mm});
            skCircle(sketch, "E5.1.13.0", {"center": v(-60, 780) * mm, "radius": 18.5 * mm});
            skCircle(sketch, "E5.2.1.0", {"center": v(-120, 60) * mm, "radius": 18.5 * mm});
            skCircle(sketch, "E5.2.2.0", {"center": v(-120, 120) * mm, "radius": 18.5 * mm});
            skCircle(sketch, "E5.2.3.0", {"center": v(-120, 180) * mm, "radius": 18.5 * mm});
            skCircle(sketch, "E5.2.4.0", {"center": v(-120, 240) * mm, "radius": 18.5 * mm});
            skCircle(sketch, "E5.2.5.0", {"center": v(-120, 300) * mm, "radius": 18.5 * mm});
            skCircle(sketch, "E5.2.6.0", {"center": v(-120, 360) * mm, "radius": 18.5 * mm});
            skCircle(sketch, "E5.2.7.0", {"center": v(-120, 420) * mm, "radius": 18.5 * mm});
            skCircle(sketch, "E5.2.8.0", {"center": v(-120, 480) * mm, "radius": 18.5 * mm});
            skCircle(sketch, "E5.2.9.0", {"center": v(-120, 540) * mm, "radius": 18.5 * mm});
            skCircle(sketch, "E5.2.10.0", {"center": v(-120, 600) * mm, "radius": 18.5 * mm});
            skCircle(sketch, "E5.2.11.0", {"center": v(-120, 660) * mm, "radius": 18.5 * mm});
            skCircle(sketch, "E5.2.12.0", {"center": v(-120, 720) * mm, "radius": 18.5 * mm});
            skCircle(sketch, "E5.2.13.0", {"center": v(-120, 780) * mm, "radius": 18.5 * mm});
            skCircle(sketch, "E5.3.1.0", {"center": v(-180, 60) * mm, "radius": 18.5 * mm});
            skCircle(sketch, "E5.3.2.0", {"center": v(-180, 120) * mm, "radius": 18.5 * mm});
            skCircle(sketch, "E5.3.3.0", {"center": v(-180, 180) * mm, "radius": 18.5 * mm});
            skCircle(sketch, "E5.3.4.0", {"center": v(-180, 240) * mm, "radius": 18.5 * mm});
            skCircle(sketch, "E5.3.5.0", {"center": v(-180, 300) * mm, "radius": 18.5 * mm});
            skCircle(sketch, "E5.3.6.0", {"center": v(-180, 360) * mm, "radius": 18.5 * mm});
            skCircle(sketch, "E5.3.7.0", {"center": v(-180, 420) * mm, "radius": 18.5 * mm});
            skCircle(sketch, "E5.3.8.0", {"center": v(-180, 480) * mm, "radius": 18.5 * mm});
            skCircle(sketch, "E5.3.9.0", {"center": v(-180, 540) * mm, "radius": 18.5 * mm});
            skCircle(sketch, "E5.3.10.0", {"center": v(-180, 600) * mm, "radius": 18.5 * mm});
            skCircle(sketch, "E5.3.11.0", {"center": v(-180, 660) * mm, "radius": 18.5 * mm});
            skCircle(sketch, "E5.3.12.0", {"center": v(-180, 720) * mm, "radius": 18.5 * mm});
            skCircle(sketch, "E5.3.13.0", {"center": v(-180, 780) * mm, "radius": 18.5 * mm});
            skCircle(sketch, "E5.4.1.0", {"center": v(-240, 60) * mm, "radius": 18.5 * mm});
            skCircle(sketch, "E5.4.2.0", {"center": v(-240, 120) * mm, "radius": 18.5 * mm});
            skCircle(sketch, "E5.4.3.0", {"center": v(-240, 180) * mm, "radius": 18.5 * mm});
            skCircle(sketch, "E5.4.4.0", {"center": v(-240, 240) * mm, "radius": 18.5 * mm});
            skCircle(sketch, "E5.4.5.0", {"center": v(-240, 300) * mm, "radius": 18.5 * mm});
            skCircle(sketch, "E5.4.6.0", {"center": v(-240, 360) * mm, "radius": 18.5 * mm});
            skCircle(sketch, "E5.4.7.0", {"center": v(-240, 420) * mm, "radius": 18.5 * mm});
            skCircle(sketch, "E5.4.8.0", {"center": v(-240, 480) * mm, "radius": 18.5 * mm});
            skCircle(sketch, "E5.4.9.0", {"center": v(-240, 540) * mm, "radius": 18.5 * mm});
            skCircle(sketch, "E5.4.10.0", {"center": v(-240, 600) * mm, "radius": 18.5 * mm});
            skCircle(sketch, "E5.4.11.0", {"center": v(-240, 660) * mm, "radius": 18.5 * mm});
            skCircle(sketch, "E5.4.12.0", {"center": v(-240, 720) * mm, "radius": 18.5 * mm});
            skCircle(sketch, "E5.4.13.0", {"center": v(-240, 780) * mm, "radius": 18.5 * mm});
            skCircle(sketch, "E5.5.1.0", {"center": v(-300, 60) * mm, "radius": 18.5 * mm});
            skCircle(sketch, "E5.5.2.0", {"center": v(-300, 120) * mm, "radius": 18.5 * mm});
            skCircle(sketch, "E5.5.3.0", {"center": v(-300, 180) * mm, "radius": 18.5 * mm});
            skCircle(sketch, "E5.5.4.0", {"center": v(-300, 240) * mm, "radius": 18.5 * mm});
            skCircle(sketch, "E5.5.5.0", {"center": v(-300, 300) * mm, "radius": 18.5 * mm});
            skCircle(sketch, "E5.5.6.0", {"center": v(-300, 360) * mm, "radius": 18.5 * mm});
            skCircle(sketch, "E5.5.7.0", {"center": v(-300, 420) * mm, "radius": 18.5 * mm});
            skCircle(sketch, "E5.5.8.0", {"center": v(-300, 480) * mm, "radius": 18.5 * mm});
            skCircle(sketch, "E5.5.9.0", {"center": v(-300, 540) * mm, "radius": 18.5 * mm});
            skCircle(sketch, "E5.5.10.0", {"center": v(-300, 600) * mm, "radius": 18.5 * mm});
            skCircle(sketch, "E5.5.11.0", {"center": v(-300, 660) * mm, "radius": 18.5 * mm});
            skCircle(sketch, "E5.5.12.0", {"center": v(-300, 720) * mm, "radius": 18.5 * mm});
            skCircle(sketch, "E5.6.1.0", {"center": v(-360, 60) * mm, "radius": 18.5 * mm});
            skCircle(sketch, "E5.6.2.0", {"center": v(-360, 120) * mm, "radius": 18.5 * mm});
            skCircle(sketch, "E5.6.3.0", {"center": v(-360, 180) * mm, "radius": 18.5 * mm});
            skCircle(sketch, "E5.6.4.0", {"center": v(-360, 240) * mm, "radius": 18.5 * mm});
            skCircle(sketch, "E5.6.5.0", {"center": v(-360, 300) * mm, "radius": 18.5 * mm});
            skCircle(sketch, "E5.6.6.0", {"center": v(-360, 360) * mm, "radius": 18.5 * mm});
            skCircle(sketch, "E5.6.7.0", {"center": v(-360, 420) * mm, "radius": 18.5 * mm});
            skCircle(sketch, "E5.6.8.0", {"center": v(-360, 480) * mm, "radius": 18.5 * mm});
            skCircle(sketch, "E5.6.9.0", {"center": v(-360, 540) * mm, "radius": 18.5 * mm});
            skCircle(sketch, "E5.6.10.0", {"center": v(-360, 600) * mm, "radius": 18.5 * mm});
            skCircle(sketch, "E5.6.11.0", {"center": v(-360, 660) * mm, "radius": 18.5 * mm});
            skCircle(sketch, "E5.6.12.0", {"center": v(-360, 720) * mm, "radius": 18.5 * mm});
            skCircle(sketch, "E5.7.1.0", {"center": v(-420, 60) * mm, "radius": 18.5 * mm});
            skCircle(sketch, "E5.7.2.0", {"center": v(-420, 120) * mm, "radius": 18.5 * mm});
            skCircle(sketch, "E5.7.3.0", {"center": v(-420, 180) * mm, "radius": 18.5 * mm});
            skCircle(sketch, "E5.7.4.0", {"center": v(-420, 240) * mm, "radius": 18.5 * mm});
            skCircle(sketch, "E5.7.5.0", {"center": v(-420, 300) * mm, "radius": 18.5 * mm});
            skCircle(sketch, "E5.7.6.0", {"center": v(-420, 360) * mm, "radius": 18.5 * mm});
            skCircle(sketch, "E5.7.7.0", {"center": v(-420, 420) * mm, "radius": 18.5 * mm});
            skCircle(sketch, "E5.7.8.0", {"center": v(-420, 480) * mm, "radius": 18.5 * mm});
            skCircle(sketch, "E5.7.9.0", {"center": v(-420, 540) * mm, "radius": 18.5 * mm});
            skCircle(sketch, "E5.7.10.0", {"center": v(-420, 600) * mm, "radius": 18.5 * mm});
            skCircle(sketch, "E5.7.11.0", {"center": v(-420, 660) * mm, "radius": 18.5 * mm});
            skCircle(sketch, "E5.8.1.0", {"center": v(-480, 60) * mm, "radius": 18.5 * mm});
            skCircle(sketch, "E5.8.2.0", {"center": v(-480, 120) * mm, "radius": 18.5 * mm});
            skCircle(sketch, "E5.8.3.0", {"center": v(-480, 180) * mm, "radius": 18.5 * mm});
            skCircle(sketch, "E5.8.4.0", {"center": v(-480, 240) * mm, "radius": 18.5 * mm});
            skCircle(sketch, "E5.8.5.0", {"center": v(-480, 300) * mm, "radius": 18.5 * mm});
            skCircle(sketch, "E5.8.6.0", {"center": v(-480, 360) * mm, "radius": 18.5 * mm});
            skCircle(sketch, "E5.8.7.0", {"center": v(-480, 420) * mm, "radius": 18.5 * mm});
            skCircle(sketch, "E5.8.8.0", {"center": v(-480, 480) * mm, "radius": 18.5 * mm});
            skCircle(sketch, "E5.8.9.0", {"center": v(-480, 540) * mm, "radius": 18.5 * mm});
            skCircle(sketch, "E5.8.10.0", {"center": v(-480, 600) * mm, "radius": 18.5 * mm});
            skCircle(sketch, "E5.9.1.0", {"center": v(-540, 60) * mm, "radius": 18.5 * mm});
            skCircle(sketch, "E5.9.2.0", {"center": v(-540, 120) * mm, "radius": 18.5 * mm});
            skCircle(sketch, "E5.9.3.0", {"center": v(-540, 180) * mm, "radius": 18.5 * mm});
            skCircle(sketch, "E5.9.4.0", {"center": v(-540, 240) * mm, "radius": 18.5 * mm});
            skCircle(sketch, "E5.9.5.0", {"center": v(-540, 300) * mm, "radius": 18.5 * mm});
            skCircle(sketch, "E5.9.6.0", {"center": v(-540, 360) * mm, "radius": 18.5 * mm});
            skCircle(sketch, "E5.9.7.0", {"center": v(-540, 420) * mm, "radius": 18.5 * mm});
            skCircle(sketch, "E5.9.8.0", {"center": v(-540, 480) * mm, "radius": 18.5 * mm});
            skCircle(sketch, "E5.9.9.0", {"center": v(-540, 540) * mm, "radius": 18.5 * mm});
            skCircle(sketch, "E5.10.1.0", {"center": v(-600, 60) * mm, "radius": 18.5 * mm});
            skCircle(sketch, "E5.10.2.0", {"center": v(-600, 120) * mm, "radius": 18.5 * mm});
            skCircle(sketch, "E5.10.3.0", {"center": v(-600, 180) * mm, "radius": 18.5 * mm});
            skCircle(sketch, "E5.10.4.0", {"center": v(-600, 240) * mm, "radius": 18.5 * mm});
            skCircle(sketch, "E5.10.5.0", {"center": v(-600, 300) * mm, "radius": 18.5 * mm});
            skCircle(sketch, "E5.10.6.0", {"center": v(-600, 360) * mm, "radius": 18.5 * mm});
            skCircle(sketch, "E5.10.7.0", {"center": v(-600, 420) * mm, "radius": 18.5 * mm});
            skCircle(sketch, "E5.10.8.0", {"center": v(-600, 480) * mm, "radius": 18.5 * mm});
            skCircle(sketch, "E5.11.1.0", {"center": v(-660, 60) * mm, "radius": 18.5 * mm});
            skCircle(sketch, "E5.11.2.0", {"center": v(-660, 120) * mm, "radius": 18.5 * mm});
            skCircle(sketch, "E5.11.3.0", {"center": v(-660, 180) * mm, "radius": 18.5 * mm});
            skCircle(sketch, "E5.11.4.0", {"center": v(-660, 240) * mm, "radius": 18.5 * mm});
            skCircle(sketch, "E5.11.5.0", {"center": v(-660, 300) * mm, "radius": 18.5 * mm});
            skCircle(sketch, "E5.11.6.0", {"center": v(-660, 360) * mm, "radius": 18.5 * mm});
            skCircle(sketch, "E5.11.7.0", {"center": v(-660, 420) * mm, "radius": 18.5 * mm});
            skCircle(sketch, "E5.12.1.0", {"center": v(-720, 60) * mm, "radius": 18.5 * mm});
            skCircle(sketch, "E5.12.2.0", {"center": v(-720, 120) * mm, "radius": 18.5 * mm});
            skCircle(sketch, "E5.12.3.0", {"center": v(-720, 180) * mm, "radius": 18.5 * mm});
            skCircle(sketch, "E5.12.4.0", {"center": v(-720, 240) * mm, "radius": 18.5 * mm});
            skCircle(sketch, "E5.12.5.0", {"center": v(-720, 300) * mm, "radius": 18.5 * mm});
            skCircle(sketch, "E5.12.6.0", {"center": v(-720, 360) * mm, "radius": 18.5 * mm});
            skCircle(sketch, "E5.13.1.0", {"center": v(-780, 60) * mm, "radius": 18.5 * mm});
            skCircle(sketch, "E5.13.2.0", {"center": v(-780, 120) * mm, "radius": 18.5 * mm});
            skCircle(sketch, "E5.13.3.0", {"center": v(-780, 180) * mm, "radius": 18.5 * mm});
            skLineSegment(sketch, "E5.direction1", {"start": v(0, 0) * mm, "end": v(-60, 0) * mm, "construction": true});
            skLineSegment(sketch, "E5.direction2", {"start": v(0, 60) * mm, "end": v(0, 0) * mm, "construction": true});
            skSolve(sketch);
        }
        {
            var Q0;
            Q0=makeQuery(id+"F2.imprint","IMPRINT",FACE,{"disambiguationData":[TD([[makeQuery(id+"F2.imprint","IMPRINT",EDGE,{"derivedFrom":sQuery(id+"F2.wireOp",EDGE,"E1")}),-1.0]])]});
            extrude(context, id + "F3", {"entities" : qUnion([Q0]), "operationType" : NewBodyOperationType.INTERSECT, "oppositeDirection" : true, "depth" : 500 * mm});
        }
    });
